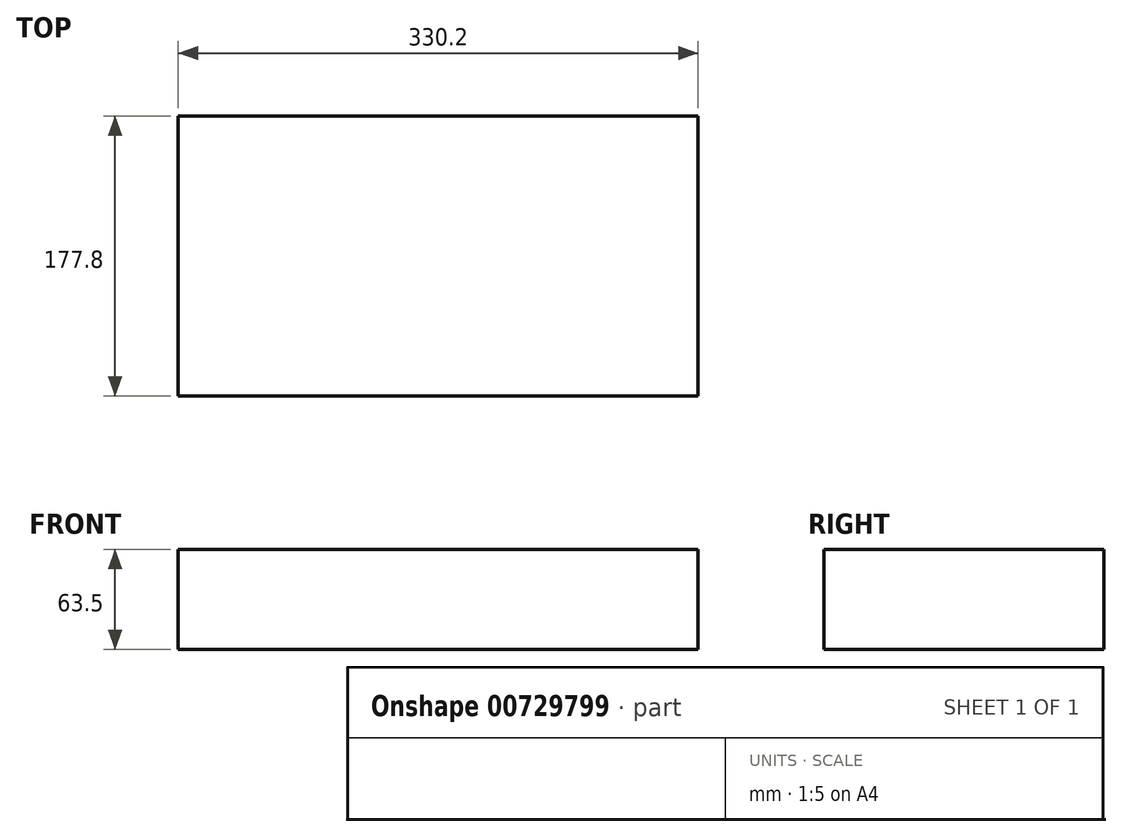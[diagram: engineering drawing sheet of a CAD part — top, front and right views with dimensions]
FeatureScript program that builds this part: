
annotation { "Feature Type Name" : "Feature", "Feature Type Description" : "" }
export const myFeature = defineFeature(function(context is Context, id is Id, definition is map)
    precondition{}
    {
        {
            var Q0;
            Q0=qCreatedBy(makeId("Top.planeOp"),FACE);
            var sketch = newSketch(context, id + "F0", { "sketchPlane" : qUnion([Q0])});
            skLineSegment(sketch, "E0.bottom", {"start": v(165.1, -88.9) * mm, "end": v(-165.1, -88.9) * mm});
            skLineSegment(sketch, "E0.top", {"start": v(165.1, 88.9) * mm, "end": v(-165.1, 88.9) * mm});
            skLineSegment(sketch, "E0.left", {"start": v(165.1, -88.9) * mm, "end": v(165.1, 88.9) * mm});
            skLineSegment(sketch, "E0.right", {"start": v(-165.1, -88.9) * mm, "end": v(-165.1, 88.9) * mm});
            skPoint(sketch, "E0.middle", {"position": v(0, 0) * mm});
            skPoint(sketch, "E1.MirrorP", {"position": v(0, -177.8) * mm});
            skSolve(sketch);
        }
        {
            var Q0;
            Q0 = qSketchRegion(id + "F0", true);
            extrude(context, id + "F1", {"entities" : qUnion([Q0]), "depth" : 63.5 * mm, "offsetDistance" : 25.4 * mm});
        }
    });
